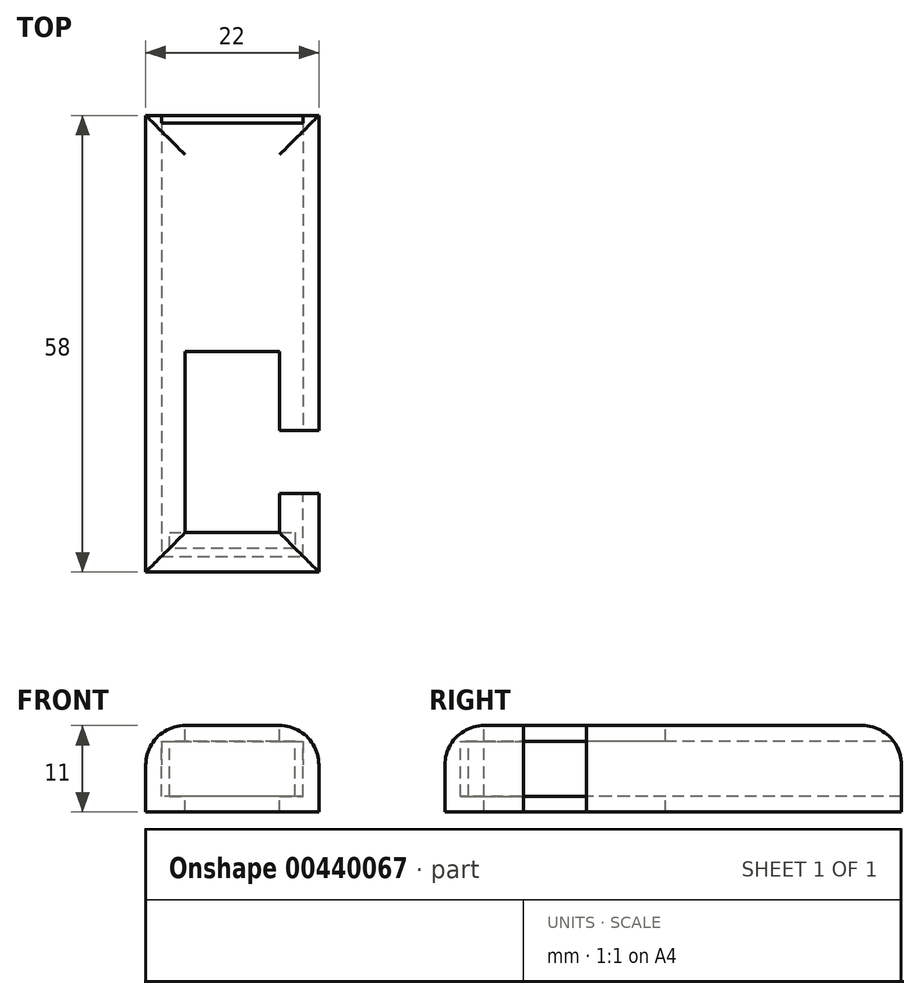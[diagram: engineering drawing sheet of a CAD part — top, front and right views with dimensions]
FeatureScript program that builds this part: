
annotation { "Feature Type Name" : "Feature", "Feature Type Description" : "" }
export const myFeature = defineFeature(function(context is Context, id is Id, definition is map)
    precondition{}
    {
        {
            var Q0;
            Q0=qCreatedBy(makeId("Top.planeOp"),FACE);
            var sketch = newSketch(context, id + "F0", { "sketchPlane" : qUnion([Q0])});
            skPoint(sketch, "E0", {"position": v(0, 25) * mm});
            skPoint(sketch, "E1", {"position": v(0, -15) * mm});
            skPoint(sketch, "E2", {"position": v(11, 25) * mm});
            skLineSegment(sketch, "E3", {"start": v(11, 25) * mm, "end": v(-11, 25) * mm});
            skLineSegment(sketch, "E4", {"start": v(11, 25) * mm, "end": v(11, -15) * mm});
            skLineSegment(sketch, "E5", {"start": v(-11, 25) * mm, "end": v(-11, -33) * mm});
            skLineSegment(sketch, "E6", {"start": v(-11, -33) * mm, "end": v(11, -33) * mm});
            skLineSegment(sketch, "E7", {"start": v(11, -33) * mm, "end": v(11, -23) * mm});
            skLineSegment(sketch, "E8", {"start": v(11, -23) * mm, "end": v(6, -23) * mm});
            skLineSegment(sketch, "E9", {"start": v(6, -23) * mm, "end": v(6, -28) * mm});
            skLineSegment(sketch, "E10", {"start": v(6, -28) * mm, "end": v(-6, -28) * mm});
            skLineSegment(sketch, "E11", {"start": v(-6, -28) * mm, "end": v(-6, -15) * mm});
            skLineSegment(sketch, "E12", {"start": v(11, -15) * mm, "end": v(6, -15) * mm});
            skPoint(sketch, "E13.start.orphan", {"position": v(0, 0) * mm});
            skPoint(sketch, "E14.MirrorCS.end.orphan", {"position": v(6, -15) * mm});
            skLineSegment(sketch, "E15", {"start": v(-6, -15) * mm, "end": v(-6, -5) * mm});
            skLineSegment(sketch, "E16", {"start": v(-6, -5) * mm, "end": v(6, -5) * mm});
            skLineSegment(sketch, "E17", {"start": v(6, -5) * mm, "end": v(6, -15) * mm});
            skSolve(sketch);
        }
        {
            var Q0;
            Q0=makeQuery(id+"F0.imprint","IMPRINT",FACE,{"disambiguationData":[TD([[makeQuery(id+"F0.imprint","IMPRINT",EDGE,{"derivedFrom":sQuery(id+"F0.wireOp",EDGE,"E3")}),1.0]])]});
            extrude(context, id + "F1", {"entities" : qUnion([Q0]), "oppositeDirection" : true, "depth" : 11 * mm});
        }
        {
            var Q0;
            Q0=makeQuery(id+"F1.opExtrude","SWEPT_FACE",FACE,{"disambiguationData":[OSD([sQuery(id+"F0.wireOp",EDGE,"E3")])]});
            shell(context, id + "F2", {"entities" : qUnion([Q0]), "thickness" : 2 * mm});
        }
        {
            var Q0;
            Q0=makeQuery(id+"F2.opShell","OFFSET_FACE",FACE,{"disambiguationData":[OSD([sQuery(id+"F0.wireOp",EDGE,"E16")])]});
            extrude(context, id + "F3", {"entities" : qUnion([Q0]), "operationType" : NewBodyOperationType.REMOVE, "oppositeDirection" : true, "depth" : 25 * mm});
        }
        {
            var Q0;
            {var subQ0=sQuery(id+"F0.wireOp",EDGE,"E17");var subQ1=sQuery(id+"F0.wireOp",EDGE,"E16");var subQ3=sQuery(id+"F0.wireOp",EDGE,"E12");Q0=makeQuery(id+"F3.boolean.opBoolean","COPY",FACE,{"disambiguationData":[TD([makeQuery(id+"F1.opExtrude","SWEPT_FACE",FACE,{"disambiguationData":[OSD([subQ3])]})])],"derivedFrom":makeQuery(id+"F3.opExtrude","SWEPT_FACE",FACE,{"disambiguationData":[OSD([subQ1,subQ0])]})});}
            extrude(context, id + "F4", {"entities" : qUnion([Q0]), "operationType" : NewBodyOperationType.ADD, "oppositeDirection" : true, "depth" : 2 * mm});
        }
        {
            var Q0;
            {var subQ0=sQuery(id+"F0.wireOp",EDGE,"E17");var subQ1=sQuery(id+"F0.wireOp",EDGE,"E16");var subQ3=sQuery(id+"F0.wireOp",EDGE,"E12");Q0=makeQuery(id+"F3.boolean.opBoolean","COPY",FACE,{"disambiguationData":[TD([makeQuery(id+"F1.opExtrude","SWEPT_FACE",FACE,{"disambiguationData":[OSD([subQ3])]})])],"derivedFrom":makeQuery(id+"F3.opExtrude","SWEPT_FACE",FACE,{"disambiguationData":[OSD([subQ1,subQ0])]})});}
            extrude(context, id + "F5", {"entities" : qUnion([Q0]), "operationType" : NewBodyOperationType.ADD, "oppositeDirection" : true, "depth" : 2 * mm});
        }
        {
            var Q0;
            {var subQ0=sQuery(id+"F0.wireOp",EDGE,"E17");var subQ1=sQuery(id+"F0.wireOp",EDGE,"E16");var subQ3=sQuery(id+"F0.wireOp",EDGE,"E12");Q0=makeQuery(id+"F3.boolean.opBoolean","COPY",FACE,{"disambiguationData":[TD([makeQuery(id+"F1.opExtrude","SWEPT_FACE",FACE,{"disambiguationData":[OSD([subQ3])]})])],"derivedFrom":makeQuery(id+"F3.opExtrude","SWEPT_FACE",FACE,{"disambiguationData":[OSD([subQ1,subQ0])]})});}
            var Q1;
            {var subQ0=sQuery(id+"F0.wireOp",EDGE,"E17");var subQ1=sQuery(id+"F0.wireOp",EDGE,"E16");var subQ7=sQuery(id+"F0.wireOp",EDGE,"E8");Q1=makeQuery(id+"F3.boolean.opBoolean","COPY",FACE,{"disambiguationData":[TD([makeQuery(id+"F1.opExtrude","SWEPT_FACE",FACE,{"disambiguationData":[OSD([subQ7])]})])],"derivedFrom":makeQuery(id+"F3.opExtrude","SWEPT_FACE",FACE,{"disambiguationData":[OSD([subQ1,subQ0])]})});}
            extrude(context, id + "F6", {"entities" : qUnion([Q0, Q1]), "operationType" : NewBodyOperationType.REMOVE, "oppositeDirection" : true, "depth" : 1 * mm});
        }
        {
            var Q0;
            Q0=makeQuery(id+"F1.opExtrude","CAP_EDGE",EDGE,{"disambiguationData":[OSD([sQuery(id+"F0.wireOp",EDGE,"E4")])],"isStart":true});
            var Q1;
            Q1=makeQuery(id+"F1.opExtrude","CAP_EDGE",EDGE,{"disambiguationData":[OSD([sQuery(id+"F0.wireOp",EDGE,"E3")])],"isStart":true});
            var Q2;
            Q2=makeQuery(id+"F1.opExtrude","CAP_EDGE",EDGE,{"disambiguationData":[OSD([sQuery(id+"F0.wireOp",EDGE,"E5")])],"isStart":true});
            var Q3;
            Q3=makeQuery(id+"F1.opExtrude","CAP_EDGE",EDGE,{"disambiguationData":[OSD([sQuery(id+"F0.wireOp",EDGE,"E6")])],"isStart":true});
            var Q4;
            Q4=makeQuery(id+"F1.opExtrude","CAP_EDGE",EDGE,{"disambiguationData":[OSD([sQuery(id+"F0.wireOp",EDGE,"E7")])],"isStart":true});
            fillet(context, id + "F7", {"entities" : qUnion([Q0, Q1, Q2, Q3, Q4]), "radius" : 5 * mm, "tangentPropagation" : true, "allowEdgeOverflow" : false});
        }
    });
